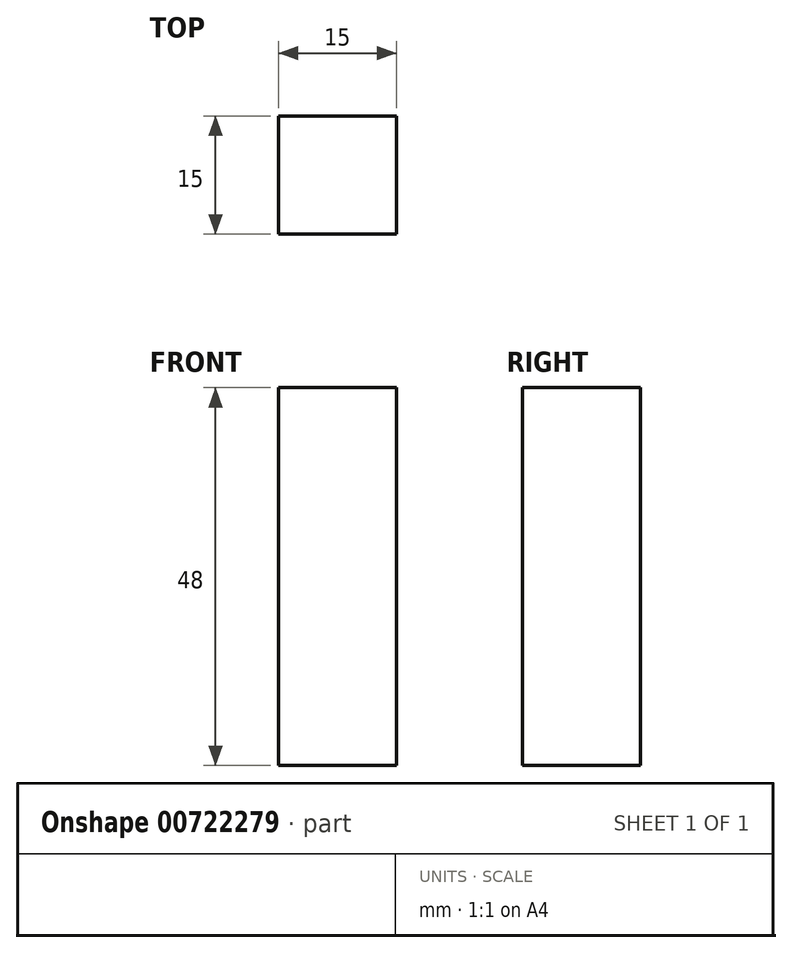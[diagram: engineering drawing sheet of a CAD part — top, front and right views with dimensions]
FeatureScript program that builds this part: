
annotation { "Feature Type Name" : "Feature", "Feature Type Description" : "" }
export const myFeature = defineFeature(function(context is Context, id is Id, definition is map)
    precondition{}
    {
        {
            var Q0;
            Q0=qCreatedBy(makeId("Front.planeOp"),FACE);
            var sketch = newSketch(context, id + "F0", { "sketchPlane" : qUnion([Q0])});
            skLineSegment(sketch, "E0.bottom", {"start": v(-77.17, 29.71) * mm, "end": v(-62.17, 29.71) * mm});
            skLineSegment(sketch, "E0.top", {"start": v(-77.17, -18.29) * mm, "end": v(-62.17, -18.29) * mm});
            skLineSegment(sketch, "E0.left", {"start": v(-77.17, 29.71) * mm, "end": v(-77.17, -18.29) * mm});
            skLineSegment(sketch, "E0.right", {"start": v(-62.17, 29.71) * mm, "end": v(-62.17, -18.29) * mm});
            skSolve(sketch);
        }
        {
            var Q0;
            Q0=makeQuery(id+"F0.imprint","IMPRINT",FACE,{"disambiguationData":[TD([[makeQuery(id+"F0.imprint","IMPRINT",EDGE,{"derivedFrom":sQuery(id+"F0.wireOp",EDGE,"E0.bottom")}),-1.0]])]});
            extrude(context, id + "F1", {"entities" : qUnion([Q0]), "depth" : 15 * mm, "offsetDistance" : 25 * mm});
        }
    });
